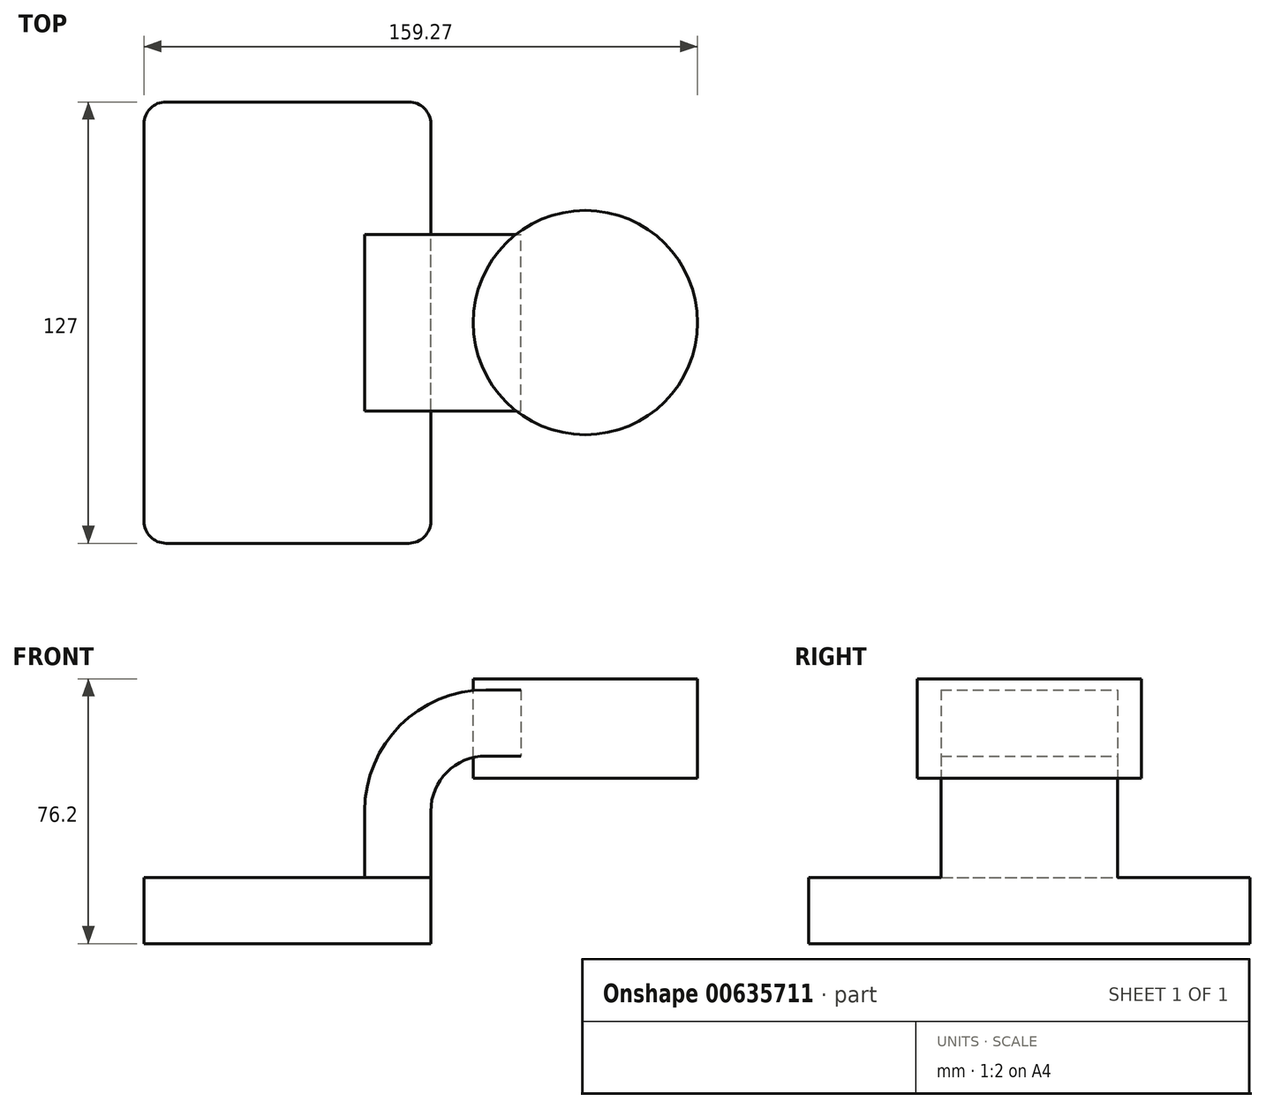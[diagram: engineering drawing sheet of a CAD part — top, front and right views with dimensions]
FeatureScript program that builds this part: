
annotation { "Feature Type Name" : "Feature", "Feature Type Description" : "" }
export const myFeature = defineFeature(function(context is Context, id is Id, definition is map)
    precondition{}
    {
        {
            var Q0;
            Q0=qCreatedBy(makeId("Front.planeOp"),FACE);
            var sketch = newSketch(context, id + "F0", { "sketchPlane" : qUnion([Q0])});
            skLineSegment(sketch, "E0.bottom", {"start": v(-28.9, 19.73) * mm, "end": v(53.65, 19.73) * mm});
            skLineSegment(sketch, "E0.top", {"start": v(-28.9, 0.68) * mm, "end": v(53.65, 0.68) * mm});
            skLineSegment(sketch, "E0.left", {"start": v(-28.9, 19.73) * mm, "end": v(-28.9, 0.68) * mm});
            skLineSegment(sketch, "E0.right", {"start": v(53.65, 19.73) * mm, "end": v(53.65, 0.68) * mm});
            skLineSegment(sketch, "E1.bottom", {"start": v(79.57, 76.88) * mm, "end": v(130.37, 76.88) * mm});
            skLineSegment(sketch, "E1.top", {"start": v(79.57, 48.3) * mm, "end": v(130.37, 48.3) * mm});
            skLineSegment(sketch, "E1.left", {"start": v(79.57, 76.88) * mm, "end": v(79.57, 48.3) * mm});
            skLineSegment(sketch, "E1.right", {"start": v(130.37, 76.88) * mm, "end": v(130.37, 48.3) * mm});
            skLineSegment(sketch, "E2", {"start": v(53.65, 19.73) * mm, "end": v(53.65, 38.78) * mm});
            skArc(sketch, "E3", {"start": v(53.65, 38.78) * mm, "mid": v(58.3, 50) * mm, "end": v(69.52, 54.66) * mm});
            skLineSegment(sketch, "E4", {"start": v(69.52, 54.66) * mm, "end": v(98.1, 54.66) * mm});
            skLineSegment(sketch, "E5.0", {"start": v(69.52, 73.7) * mm, "end": v(98.1, 73.7) * mm});
            skArc(sketch, "E5.1", {"start": v(34.6, 38.78) * mm, "mid": v(44.83, 63.48) * mm, "end": v(69.52, 73.7) * mm});
            skLineSegment(sketch, "E5.2", {"start": v(34.6, 13.38) * mm, "end": v(34.6, 38.78) * mm});
            skFitSpline(sketch, "E6", {"points": [v(-28.9, 19.73) * mm, v(69.52, 73.7) * mm], "startDerivative": vector(20.97, 77.08) * mm, "endDerivative": vector(159.72, -3.06) * mm});
            skLineSegment(sketch, "E7", {"start": v(98.1, 73.7) * mm, "end": v(98.1, 76.88) * mm});
            skLineSegment(sketch, "E8", {"start": v(98.1, 76.88) * mm, "end": v(98.1, 48.3) * mm});
            skSolve(sketch);
        }
        {
            var Q0;
            Q0=makeQuery(id+"F0.imprint","IMPRINT",FACE,{"disambiguationData":[TD([[makeQuery(id+"F0.imprint","IMPRINT",EDGE,{"derivedFrom":sQuery(id+"F0.wireOp",EDGE,"E0.top")}),1.0]])]});
            extrude(context, id + "F1", {"entities" : qUnion([Q0]), "endBound" : BoundingType.SYMMETRIC, "depth" : 127 * mm, "offsetDistance" : 25.4 * mm});
        }
        {
            var Q0;
            {var subQ1=sQuery(id+"F0.wireOp",EDGE,"E2");Q0=makeQuery(id+"F0.imprint","IMPRINT",FACE,{"disambiguationData":[TD([[makeQuery(id+"F0.imprint","IMPRINT",EDGE,{"derivedFrom":subQ1}),1.0]])]});}
            var Q1;
            {var subQ5=sQuery(id+"F0.wireOp",EDGE,"zwffYm7p-DDS7-O9gX-opt1-plTZIogGWQBk");Q1=makeQuery(id+"F0.imprint","IMPRINT",FACE,{"disambiguationData":[TD([[makeQuery(id+"F0.imprint","IMPRINT",EDGE,{"derivedFrom":subQ5}),-1.0]])]});}
            extrude(context, id + "F2", {"entities" : qUnion([Q0, Q1]), "operationType" : NewBodyOperationType.ADD, "endBound" : BoundingType.SYMMETRIC, "depth" : 50.8 * mm, "offsetDistance" : 25.4 * mm});
        }
        {
            var Q0;
            {var subQ4=sQuery(id+"F0.wireOp",EDGE,"E5.1");Q0=makeQuery(id+"F0.imprint","IMPRINT",FACE,{"disambiguationData":[TD([[makeQuery(id+"F0.imprint","IMPRINT",EDGE,{"derivedFrom":subQ4}),1.0]])]});}
            extrude(context, id + "F3", {"entities" : qUnion([Q0]), "operationType" : NewBodyOperationType.ADD, "endBound" : BoundingType.SYMMETRIC, "depth" : 15.88 * mm, "offsetDistance" : 25.4 * mm});
        }
        {
            var Q0;
            {var subQ4=sQuery(id+"F0.wireOp",EDGE,"E1.right");Q0=makeQuery(id+"F0.imprint","IMPRINT",FACE,{"disambiguationData":[TD([[makeQuery(id+"F0.imprint","IMPRINT",EDGE,{"derivedFrom":subQ4}),-1.0]])]});}
            var Q1;
            Q1=sQuery(id+"F0.wireOp",EDGE,"E8");
            revolve(context, id + "F4", {"entities" : qUnion([Q0]), "axis" : qUnion([Q1]), "revolveType" : RevolveType.FULL});
        }
        {
            var Q0;
            Q0=makeQuery(id+"F1.opExtrude","CAP_EDGE",EDGE,{"disambiguationData":[OSD([sQuery(id+"F0.wireOp",EDGE,"E0.left")])],"isStart":false});
            var Q1;
            Q1=makeQuery(id+"F1.opExtrude","CAP_EDGE",EDGE,{"disambiguationData":[OSD([sQuery(id+"F0.wireOp",EDGE,"E0.right")])],"isStart":false});
            var Q2;
            Q2=makeQuery(id+"F1.opExtrude","CAP_EDGE",EDGE,{"disambiguationData":[OSD([sQuery(id+"F0.wireOp",EDGE,"E0.left")])],"isStart":true});
            var Q3;
            Q3=makeQuery(id+"F1.opExtrude","CAP_EDGE",EDGE,{"disambiguationData":[OSD([sQuery(id+"F0.wireOp",EDGE,"E0.right")])],"isStart":true});
            fillet(context, id + "F5", {"entities" : qUnion([Q0, Q1, Q2, Q3]), "radius" : 6.35 * mm, "tangentPropagation" : true, "allowEdgeOverflow" : false});
        }
    });
